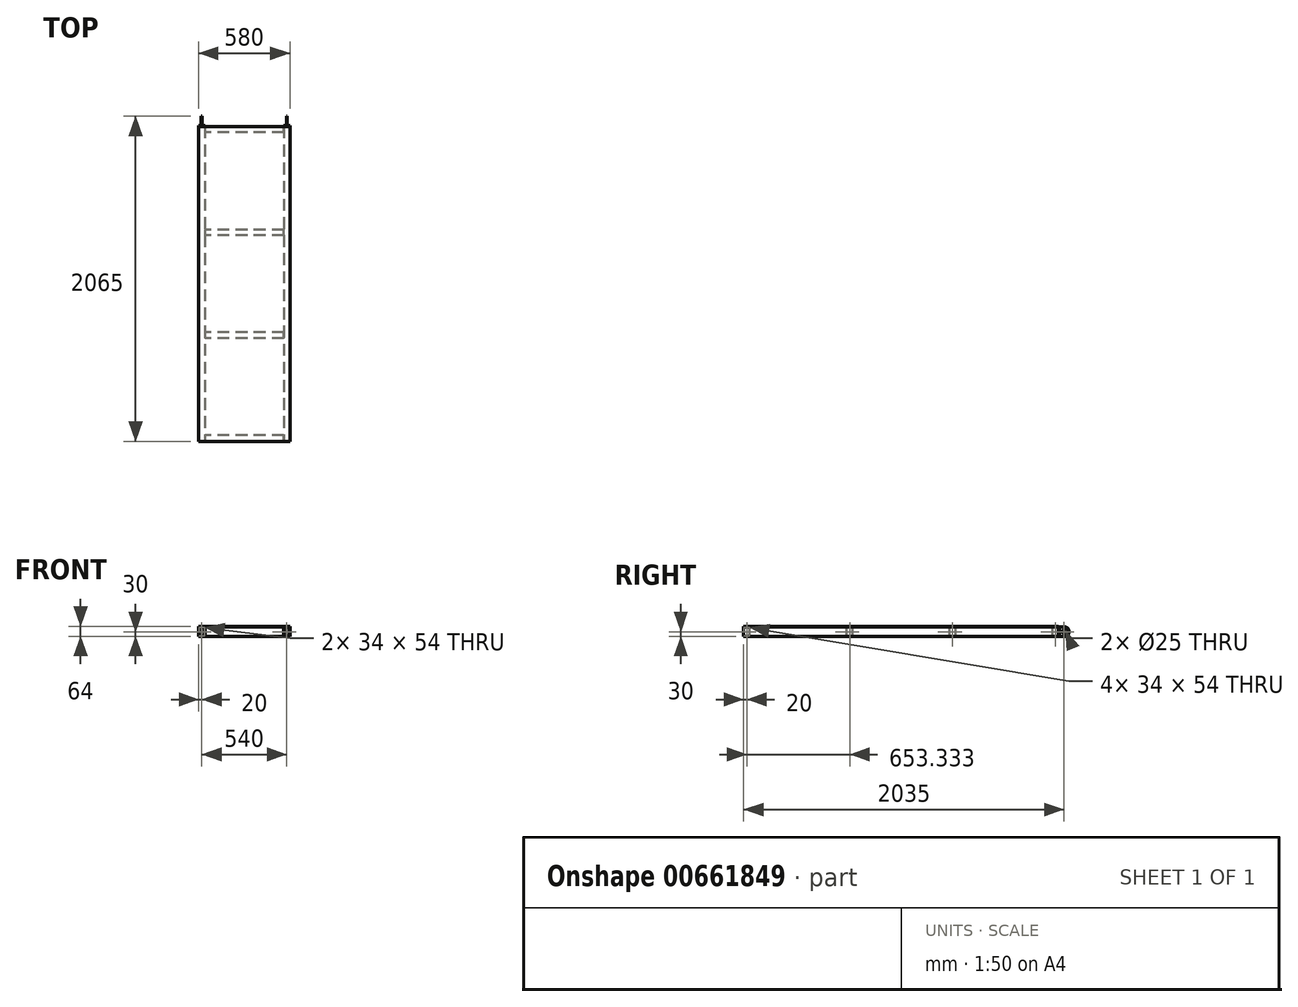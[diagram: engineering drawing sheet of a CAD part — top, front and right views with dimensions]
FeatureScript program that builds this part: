
annotation { "Feature Type Name" : "Feature", "Feature Type Description" : "" }
export const myFeature = defineFeature(function(context is Context, id is Id, definition is map)
    precondition{}
    {
        {
            var Q0;
            Q0=qCreatedBy(makeId("Front.planeOp"),FACE);
            var sketch = newSketch(context, id + "F0", { "sketchPlane" : qUnion([Q0])});
            skLineSegment(sketch, "E0", {"start": v(-250, 0) * mm, "end": v(44.05, 0) * mm, "construction": true});
            skLineSegment(sketch, "E1.bottom", {"start": v(-250, 0) * mm, "end": v(-290, 0) * mm});
            skLineSegment(sketch, "E1.top", {"start": v(-250, -60) * mm, "end": v(-290, -60) * mm});
            skLineSegment(sketch, "E1.left", {"start": v(-250, 0) * mm, "end": v(-250, -60) * mm});
            skLineSegment(sketch, "E1.right", {"start": v(-290, 0) * mm, "end": v(-290, -60) * mm});
            skLineSegment(sketch, "E2.0", {"start": v(-253, -3) * mm, "end": v(-287, -3) * mm});
            skLineSegment(sketch, "E2.1", {"start": v(-253, -3) * mm, "end": v(-253, -57) * mm});
            skLineSegment(sketch, "E2.2", {"start": v(-253, -57) * mm, "end": v(-287, -57) * mm});
            skLineSegment(sketch, "E2.3", {"start": v(-287, -3) * mm, "end": v(-287, -57) * mm});
            skLineSegment(sketch, "E3.MirrorCS", {"start": v(250, 0) * mm, "end": v(290, 0) * mm});
            skLineSegment(sketch, "E4.MirrorCS", {"start": v(250, -60) * mm, "end": v(290, -60) * mm});
            skLineSegment(sketch, "E5.MirrorCS", {"start": v(250, 0) * mm, "end": v(250, -60) * mm});
            skLineSegment(sketch, "E6.MirrorCS", {"start": v(290, 0) * mm, "end": v(290, -60) * mm});
            skLineSegment(sketch, "E7.MirrorCS", {"start": v(253, -3) * mm, "end": v(287, -3) * mm});
            skLineSegment(sketch, "E8.MirrorCS", {"start": v(287, -3) * mm, "end": v(287, -57) * mm});
            skLineSegment(sketch, "E9.MirrorCS", {"start": v(253, -3) * mm, "end": v(253, -57) * mm});
            skLineSegment(sketch, "E10.MirrorCS", {"start": v(253, -57) * mm, "end": v(287, -57) * mm});
            skSolve(sketch);
        }
        {
            var Q0;
            Q0=qSketchRegion(id+"F0",true);
            extrude(context, id + "F1", {"entities" : qUnion([Q0]), "oppositeDirection" : true, "depth" : 2000 * mm, "offsetDistance" : 25 * mm});
        }
        {
            var Q0;
            Q0=makeQuery(id+"F1.opExtrude","SWEPT_FACE",FACE,{"disambiguationData":[OSD([sQuery(id+"F0.wireOp",EDGE,"E1.left")])]});
            var sketch = newSketch(context, id + "F2", { "sketchPlane" : qUnion([Q0])});
            skLineSegment(sketch, "E11.bottom", {"start": v(0, -60) * mm, "end": v(40, -60) * mm});
            skLineSegment(sketch, "E11.top", {"start": v(0, 0) * mm, "end": v(40, 0) * mm});
            skLineSegment(sketch, "E11.left", {"start": v(0, -60) * mm, "end": v(0, 0) * mm});
            skLineSegment(sketch, "E11.right", {"start": v(40, -60) * mm, "end": v(40, 0) * mm});
            skLineSegment(sketch, "E12.0", {"start": v(3, -3) * mm, "end": v(37, -3) * mm});
            skLineSegment(sketch, "E12.1", {"start": v(3, -57) * mm, "end": v(3, -3) * mm});
            skLineSegment(sketch, "E12.2", {"start": v(3, -57) * mm, "end": v(37, -57) * mm});
            skLineSegment(sketch, "E12.3", {"start": v(37, -57) * mm, "end": v(37, -3) * mm});
            skLineSegment(sketch, "E13.1.0.0", {"start": v(656.33, -57) * mm, "end": v(690.33, -57) * mm});
            skLineSegment(sketch, "E13.1.0.1", {"start": v(656.33, -57) * mm, "end": v(656.33, -3) * mm});
            skLineSegment(sketch, "E13.1.0.2", {"start": v(656.33, -3) * mm, "end": v(690.33, -3) * mm});
            skLineSegment(sketch, "E13.1.0.3", {"start": v(693.33, -60) * mm, "end": v(693.33, 0) * mm});
            skLineSegment(sketch, "E13.1.0.4", {"start": v(653.33, -60) * mm, "end": v(653.33, 0) * mm});
            skLineSegment(sketch, "E13.1.0.5", {"start": v(653.33, 0) * mm, "end": v(693.33, 0) * mm});
            skLineSegment(sketch, "E13.1.0.6", {"start": v(653.33, -60) * mm, "end": v(693.33, -60) * mm});
            skLineSegment(sketch, "E13.1.0.7", {"start": v(690.33, -57) * mm, "end": v(690.33, -3) * mm});
            skLineSegment(sketch, "E13.2.0.0", {"start": v(1309.67, -57) * mm, "end": v(1343.67, -57) * mm});
            skLineSegment(sketch, "E13.2.0.1", {"start": v(1309.67, -57) * mm, "end": v(1309.67, -3) * mm});
            skLineSegment(sketch, "E13.2.0.2", {"start": v(1309.67, -3) * mm, "end": v(1343.67, -3) * mm});
            skLineSegment(sketch, "E13.2.0.3", {"start": v(1346.67, -60) * mm, "end": v(1346.67, 0) * mm});
            skLineSegment(sketch, "E13.2.0.4", {"start": v(1306.67, -60) * mm, "end": v(1306.67, 0) * mm});
            skLineSegment(sketch, "E13.2.0.5", {"start": v(1306.67, 0) * mm, "end": v(1346.67, 0) * mm});
            skLineSegment(sketch, "E13.2.0.6", {"start": v(1306.67, -60) * mm, "end": v(1346.67, -60) * mm});
            skLineSegment(sketch, "E13.2.0.7", {"start": v(1343.67, -57) * mm, "end": v(1343.67, -3) * mm});
            skLineSegment(sketch, "E13.3.0.0", {"start": v(1963, -57) * mm, "end": v(1997, -57) * mm});
            skLineSegment(sketch, "E13.3.0.1", {"start": v(1963, -57) * mm, "end": v(1963, -3) * mm});
            skLineSegment(sketch, "E13.3.0.2", {"start": v(1963, -3) * mm, "end": v(1997, -3) * mm});
            skLineSegment(sketch, "E13.3.0.3", {"start": v(2000, -60) * mm, "end": v(2000, 0) * mm});
            skLineSegment(sketch, "E13.3.0.4", {"start": v(1960, -60) * mm, "end": v(1960, 0) * mm});
            skLineSegment(sketch, "E13.3.0.5", {"start": v(1960, 0) * mm, "end": v(2000, 0) * mm});
            skLineSegment(sketch, "E13.3.0.6", {"start": v(1960, -60) * mm, "end": v(2000, -60) * mm});
            skLineSegment(sketch, "E13.3.0.7", {"start": v(1997, -57) * mm, "end": v(1997, -3) * mm});
            skLineSegment(sketch, "E13.direction1", {"start": v(0, -60) * mm, "end": v(653.33, -60) * mm, "construction": true});
            skSolve(sketch);
        }
        {
            var Q0;
            Q0=qSketchRegion(id+"F2",true);
            extrude(context, id + "F3", {"entities" : qUnion([Q0]), "depth" : 500 * mm, "offsetDistance" : 25 * mm});
        }
        {
            var Q0;
            Q0=makeQuery(id+"F1.opExtrude","SWEPT_FACE",FACE,{"disambiguationData":[OSD([sQuery(id+"F0.wireOp",EDGE,"E1.bottom")])]});
            var sketch = newSketch(context, id + "F4", { "sketchPlane" : qUnion([Q0])});
            skLineSegment(sketch, "E14.0", {"start": v(-290, 2000) * mm, "end": v(-290, 0) * mm});
            skLineSegment(sketch, "E15.0", {"start": v(-250, 0) * mm, "end": v(-290, 0) * mm});
            skLineSegment(sketch, "E16.0", {"start": v(250, 0) * mm, "end": v(-250, 0) * mm});
            skLineSegment(sketch, "E17.0", {"start": v(290, 2000) * mm, "end": v(290, 0) * mm});
            skLineSegment(sketch, "E18.0", {"start": v(250, 0) * mm, "end": v(290, 0) * mm});
            skLineSegment(sketch, "E19.0", {"start": v(250, 2000) * mm, "end": v(-250, 2000) * mm});
            skLineSegment(sketch, "E20.0", {"start": v(250, 2000) * mm, "end": v(290, 2000) * mm});
            skLineSegment(sketch, "E21.0", {"start": v(-250, 2000) * mm, "end": v(-290, 2000) * mm});
            skSolve(sketch);
        }
        {
            var Q0;
            Q0=qSketchRegion(id+"F4",true);
            extrude(context, id + "F5", {"entities" : qUnion([Q0]), "depth" : 4 * mm, "offsetDistance" : 25 * mm});
        }
        {
            var Q0;
            Q0=makeQuery(id+"F1.opExtrude","SWEPT_FACE",FACE,{"disambiguationData":[OSD([sQuery(id+"F0.wireOp",EDGE,"E6.MirrorCS")])]});
            cPlane(context, id + "F6", {"entities" : qUnion([Q0]), "cplaneType" : CPlaneType.OFFSET, "offset" : 22 * mm, "oppositeDirection" : true, "width" : 150 * mm, "height" : 150 * mm});
        }
        {
            var Q0;
            Q0=makeQuery(id+"F1.opExtrude","CAP_FACE",FACE,{"disambiguationData":[OSD([sQuery(id+"F0.wireOp",EDGE,"E3.MirrorCS"),sQuery(id+"F0.wireOp",EDGE,"E4.MirrorCS"),sQuery(id+"F0.wireOp",EDGE,"E5.MirrorCS"),sQuery(id+"F0.wireOp",EDGE,"E6.MirrorCS"),sQuery(id+"F0.wireOp",EDGE,"E7.MirrorCS"),sQuery(id+"F0.wireOp",EDGE,"E8.MirrorCS"),sQuery(id+"F0.wireOp",EDGE,"E9.MirrorCS"),sQuery(id+"F0.wireOp",EDGE,"E10.MirrorCS")])],"isStart":false});
            var sketch = newSketch(context, id + "F7", { "sketchPlane" : qUnion([Q0])});
            skLineSegment(sketch, "E22.0", {"start": v(-290, 0) * mm, "end": v(290, 0) * mm});
            skLineSegment(sketch, "E23.0", {"start": v(-250, 0) * mm, "end": v(-250, -60) * mm});
            skLineSegment(sketch, "E24.0", {"start": v(-250, -60) * mm, "end": v(-290, -60) * mm});
            skLineSegment(sketch, "E25.0", {"start": v(-290, 0) * mm, "end": v(-290, -60) * mm});
            skSolve(sketch);
        }
        {
            var Q0;
            Q0=qSketchRegion(id+"F7",true);
            extrude(context, id + "F8", {"entities" : qUnion([Q0]), "depth" : 5 * mm, "offsetDistance" : 25 * mm});
        }
        {
            var Q0;
            Q0=qCreatedBy(id+"F6.planeOp",FACE);
            var sketch = newSketch(context, id + "F9", { "sketchPlane" : qUnion([Q0])});
            skLineSegment(sketch, "E26.bottom", {"start": v(2005, -60) * mm, "end": v(2040, -60) * mm});
            skLineSegment(sketch, "E26.top", {"start": v(2005, 0) * mm, "end": v(2040, 0) * mm});
            skLineSegment(sketch, "E26.left", {"start": v(2005, -60) * mm, "end": v(2005, 0) * mm});
            skLineSegment(sketch, "E26.right", {"start": v(2065, -35) * mm, "end": v(2065, -25) * mm});
            skLineSegment(sketch, "E27", {"start": v(2065, -30) * mm, "end": v(2005, -30) * mm, "construction": true});
            skLineSegment(sketch, "E28", {"start": v(2035, 0) * mm, "end": v(2035, -60) * mm, "construction": true});
            skCircle(sketch, "E29", {"center": v(2035, -30) * mm, "radius": 12.5 * mm});
            skLineSegment(sketch, "E30.0", {"start": v(2005, 0) * mm, "end": v(2005, -60) * mm});
            skPoint(sketch, "E31.visualSharp", {"position": v(2065, 0) * mm});
            skArc(sketch, "E31.filletArc", {"start": v(2065, -25) * mm, "mid": v(2057.68, -7.32) * mm, "end": v(2040, 0) * mm});
            skPoint(sketch, "E32.visualSharp", {"position": v(2065, -60) * mm});
            skArc(sketch, "E32.filletArc", {"start": v(2040, -60) * mm, "mid": v(2057.68, -52.68) * mm, "end": v(2065, -35) * mm});
            skSolve(sketch);
        }
        {
            var Q0;
            Q0=qSketchRegion(id+"F9",true);
            extrude(context, id + "F10", {"entities" : qUnion([Q0]), "operationType" : NewBodyOperationType.ADD, "depth" : 5 * mm, "offsetDistance" : 25 * mm});
        }
        {
            var Q0;
            Q0=makeQuery(id+"F10.opExtrude","SWEPT_BODY",BODY,{"disambiguationData":[OSD([sQuery(id+"F9.wireOp",EDGE,"E26.bottom"),sQuery(id+"F9.wireOp",EDGE,"E26.top"),sQuery(id+"F9.wireOp",EDGE,"E26.right"),sQuery(id+"F9.wireOp",EDGE,"E29"),sQuery(id+"F9.wireOp",EDGE,"E30.0"),sQuery(id+"F9.wireOp",EDGE,"E31.filletArc"),sQuery(id+"F9.wireOp",EDGE,"E32.filletArc")])]});
            var Q1;
            Q1=makeQuery(id+"F8.opExtrude","SWEPT_BODY",BODY,{"disambiguationData":[OSD([sQuery(id+"F7.wireOp",EDGE,"E22.0"),sQuery(id+"F7.wireOp",EDGE,"E23.0"),sQuery(id+"F7.wireOp",EDGE,"E24.0"),sQuery(id+"F7.wireOp",EDGE,"E25.0")])]});
            var Q2;
            Q2=qCreatedBy(makeId("Right.planeOp"),FACE);
            mirror(context, id + "F11", {"entities" : qUnion([Q0, Q1]), "mirrorPlane" : qUnion([Q2])});
        }
    });
